# Revit family: FU_Chair_Sandler_Momo
name_source: partatom
category: Furniture
units: mm (PartAtom-declared; Revit-internal decimal feet)

## family parameters
Always vertical = Yes
Cut with Voids When Loaded = No
OmniClass Number = 23.40.20.00
OmniClass Title = General Furniture and Specialties
Room Calculation Point = No
Shared = No
Work Plane-Based = No

## types (2) — shared parameters
Arm Width = 580 mm  [stored 1.90289 ft]
Depth = 550 mm  [stored 1.80446 ft]
Height = 810 mm
Manufacturer = Sandler
URL = https://www.sandlerseating.com
Width = 520 mm  [stored 1.70604 ft]
zero-valued in all types: Default Elevation

## per-type parameters (varying)
| type | Arms_IsVisible | Description | Frame | Momo Mesh |
| Momo 1 | No | 4-leg chair made of expanded metal mesh welded to a curved tubular galvanised steel frame, polyester powder coated. Suitable for outdoor use as well as indoor. Stackable up to 12 units. Minimum order quantity 4 and only available in Multiples of 4. | Metal - Powdercoat - Senf - NCS 2070-Y10R | Metal - Mesh - Senf - NCS 2070-Y10R |
| Momo 2 | Yes | 4-leg armchair made of expanded metal mesh welded to a curved tubular galvanised steel frame, polyester powder coated. Suitable for outdoor use as well as indoor. Stackable up to 12 units. Minimum order quantity 4 and only available in Multiples of 4. | Metal - Powdercoat - Aubergine NCS 5540-Y90R | Metal - Mesh - Aubergine NCS 5540-Y90R |

note: column(s) folded — value = type name in every type: Model

note: [stored X ft] marks values corroborated as IEEE doubles in the binary element streams (Revit-internal decimal feet)

## geometry (parser evidence)
native form markers: Sweep x6
no freeform markers — native parametric forms only
